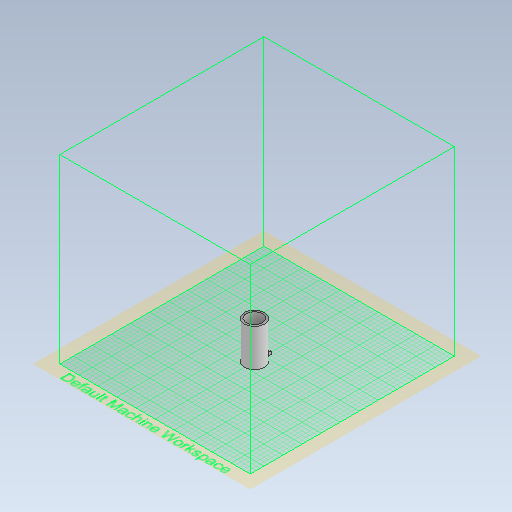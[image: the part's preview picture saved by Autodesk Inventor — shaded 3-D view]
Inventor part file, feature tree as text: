
AUTODESK INVENTOR PART (.ipt)
format: ipt  version: 2021 (Build 250183000, 183)  size: 438,784 bytes
history: native  units: in
note: dims shown in document units (in); Inventor stores cm internally (conversion verified against a paired STEP export)
features: extrude x3, sketch x3, fillet x2, chamfer x1, projected_geometry x1
ambient origin geometry x8: Origin, YZ Plane, XZ Plane, XY Plane, X Axis, Y Axis, Z Axis, Center Point
bodies: Solid1 (feature_tree)
feature tree (10):
  extrude  "Extrusion1"  Depth=3.2677in TaperAngle=0.0deg
  extrude  "Extrusion7"  Depth=3.189in TaperAngle=0.0deg
  fillet  "Fillet12"  Radius=0.3937in
  extrude  "Extrusion15"  Depth=0.6299in
  chamfer  "Chamfer8"  [1 undecoded]
  fillet  "Fillet13"  Radius=0.0787in
  sketch  "Sketch2"  dims[d2=1.752in d3=3.2677in d4=0.0in]
  sketch  "Sketch9"  dims[d54=1.4173in d55=3.189in d56=0.0in d117=0.3937in]
  projected_geometry  "Projected Loop7"
  sketch  "Sketch18"  dims[d122=0.122in d123=0.185in d124=0.0in d125=0.0in d126=0.0787in d127=0.0787in d128=45.0deg d129=0.6299in d19=0.0197in d20=0.0344in d21=0.0197in d22=0.0344in]
note: 1 required parameter value undecoded (feature->parameter linkage not recoverable at this tier; creation-order binding heuristic only, values carry confidence <= 0.55)
